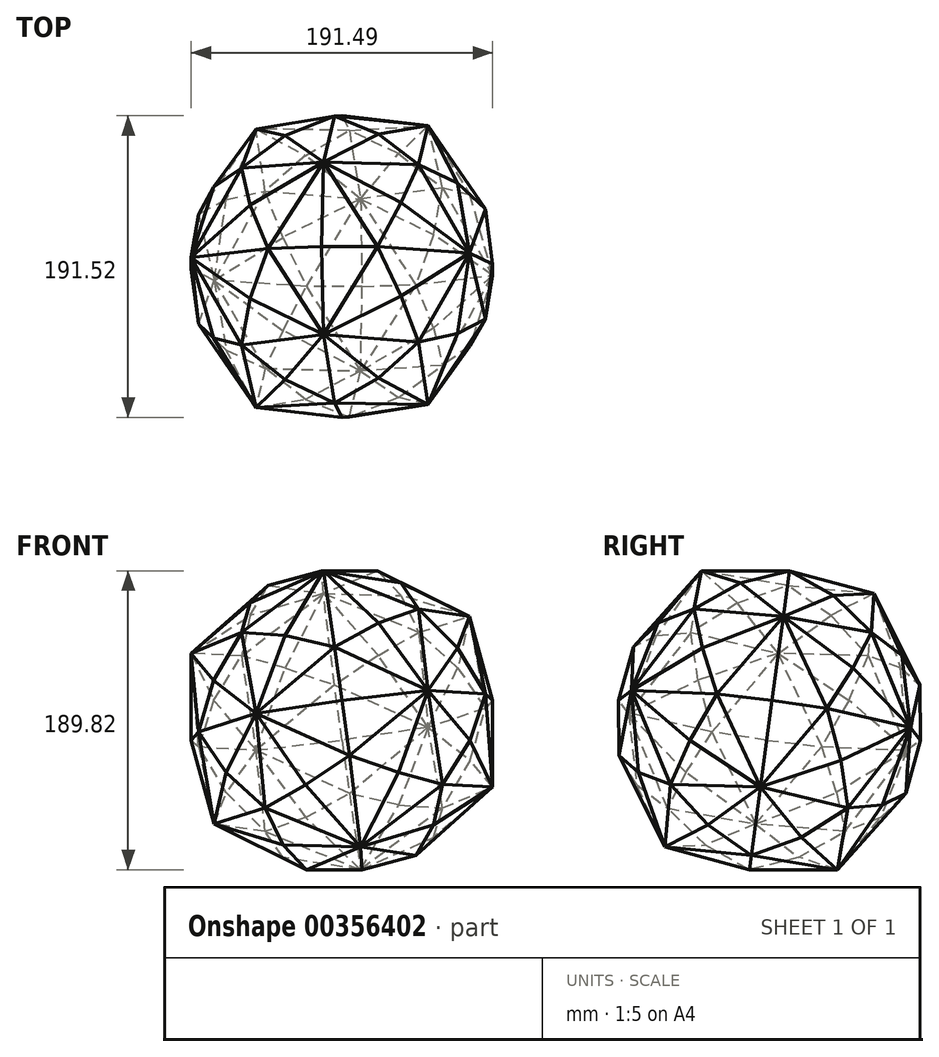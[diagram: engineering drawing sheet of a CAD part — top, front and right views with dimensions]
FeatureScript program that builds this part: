
annotation { "Feature Type Name" : "Feature", "Feature Type Description" : "" }
export const myFeature = defineFeature(function(context is Context, id is Id, definition is map)
    precondition{}
    {
        {
            var Q0;
            Q0=qCreatedBy(makeId("Top.planeOp"),FACE);
            var sketch = newSketch(context, id + "F0", { "sketchPlane" : qUnion([Q0])});
            skLineSegment(sketch, "E0", {"start": v(-0.98, 55.62) * mm, "end": v(-35.41, 0) * mm});
            skLineSegment(sketch, "E1", {"start": v(-35.41, 0) * mm, "end": v(0, 0) * mm});
            skLineSegment(sketch, "E2", {"start": v(0, 0) * mm, "end": v(-0.98, 55.62) * mm});
            skSolve(sketch);
        }
        {
            var Q0;
            Q0=makeQuery(id+"F0.imprint","IMPRINT",FACE,{"disambiguationData":[TD([[makeQuery(id+"F0.imprint","IMPRINT",EDGE,{"derivedFrom":sQuery(id+"F0.wireOp",EDGE,"E0")}),1.0]])]});
            extrude(context, id + "F1", {"entities" : qUnion([Q0]), "depth" : 101.6 * mm, "offsetDistance" : 25.4 * mm, "hasDraft" : true, "draftAngle" : 7.56 * degree, "draftPullDirection" : true});
        }
        {
            var Q0;
            Q0=makeQuery(id+"F1.opExtrude","SWEPT_BODY",BODY,{"disambiguationData":[OSD([sQuery(id+"F0.wireOp",EDGE,"E0"),sQuery(id+"F0.wireOp",EDGE,"E1"),sQuery(id+"F0.wireOp",EDGE,"E2")])]});
            var Q1;
            Q1=makeQuery(id+"F1.opExtrude","SWEPT_FACE",FACE,{"disambiguationData":[OSD([sQuery(id+"F0.wireOp",EDGE,"E0")])]});
            mirror(context, id + "F2", {"operationType" : NewBodyOperationType.ADD, "entities" : qUnion([Q0]), "mirrorPlane" : qUnion([Q1])});
        }
        {
            var Q0;
            Q0=makeQuery(id+"F1.opExtrude","SWEPT_BODY",BODY,{"disambiguationData":[OSD([sQuery(id+"F0.wireOp",EDGE,"E0"),sQuery(id+"F0.wireOp",EDGE,"E1"),sQuery(id+"F0.wireOp",EDGE,"E2")])]});
            var Q1;
            Q1=makeQuery(id+"F1.opExtrude","SWEPT_FACE",FACE,{"disambiguationData":[OSD([sQuery(id+"F0.wireOp",EDGE,"E2")])]});
            mirror(context, id + "F3", {"operationType" : NewBodyOperationType.ADD, "entities" : qUnion([Q0]), "mirrorPlane" : qUnion([Q1])});
        }
        {
            var Q0;
            Q0=makeQuery(id+"F1.opExtrude","SWEPT_BODY",BODY,{"disambiguationData":[OSD([sQuery(id+"F0.wireOp",EDGE,"E0"),sQuery(id+"F0.wireOp",EDGE,"E1"),sQuery(id+"F0.wireOp",EDGE,"E2")])]});
            var Q1;
            Q1=makeQuery(id+"F3.opPattern","COPY",FACE,{"derivedFrom":makeQuery(id+"F2.opPattern","COPY",FACE,{"derivedFrom":makeQuery(id+"F1.opExtrude","SWEPT_FACE",FACE,{"disambiguationData":[OSD([sQuery(id+"F0.wireOp",EDGE,"E2")])]}),"instanceName":"1"}),"instanceName":"1"});
            mirror(context, id + "F4", {"operationType" : NewBodyOperationType.ADD, "entities" : qUnion([Q0]), "mirrorPlane" : qUnion([Q1])});
        }
        {
            var Q0;
            Q0=makeQuery(id+"F1.opExtrude","SWEPT_BODY",BODY,{"disambiguationData":[OSD([sQuery(id+"F0.wireOp",EDGE,"E0"),sQuery(id+"F0.wireOp",EDGE,"E1"),sQuery(id+"F0.wireOp",EDGE,"E2")])]});
            var Q1;
            Q1=makeQuery(id+"F2.opPattern","COPY",FACE,{"derivedFrom":makeQuery(id+"F1.opExtrude","SWEPT_FACE",FACE,{"disambiguationData":[OSD([sQuery(id+"F0.wireOp",EDGE,"E2")])]}),"instanceName":"1"});
            mirror(context, id + "F5", {"operationType" : NewBodyOperationType.ADD, "entities" : qUnion([Q0]), "mirrorPlane" : qUnion([Q1])});
        }
        {
            var Q0;
            Q0=makeQuery(id+"F1.opExtrude","SWEPT_BODY",BODY,{"disambiguationData":[OSD([sQuery(id+"F0.wireOp",EDGE,"E0"),sQuery(id+"F0.wireOp",EDGE,"E1"),sQuery(id+"F0.wireOp",EDGE,"E2")])]});
            var Q1;
            {var subQ0=makeQuery(id+"F1.opExtrude","SWEPT_FACE",FACE,{"disambiguationData":[OSD([sQuery(id+"F0.wireOp",EDGE,"E1")])]});Q1=makeQuery(id+"F3.boolean.opBoolean","MERGE",FACE,{"derivedFrom":[subQ0,makeQuery(id+"F3.opPattern","COPY",FACE,{"derivedFrom":subQ0,"instanceName":"1"})]});}
            mirror(context, id + "F6", {"operationType" : NewBodyOperationType.ADD, "entities" : qUnion([Q0]), "mirrorPlane" : qUnion([Q1])});
        }
        {
            var Q0;
            Q0=makeQuery(id+"F1.opExtrude","SWEPT_BODY",BODY,{"disambiguationData":[OSD([sQuery(id+"F0.wireOp",EDGE,"E0"),sQuery(id+"F0.wireOp",EDGE,"E1"),sQuery(id+"F0.wireOp",EDGE,"E2")])]});
            var Q1;
            {var subQ0=makeQuery(id+"F3.opPattern","COPY",FACE,{"derivedFrom":makeQuery(id+"F2.opPattern","COPY",FACE,{"derivedFrom":makeQuery(id+"F1.opExtrude","SWEPT_FACE",FACE,{"disambiguationData":[OSD([sQuery(id+"F0.wireOp",EDGE,"E1")])]}),"instanceName":"1"}),"instanceName":"1"});Q1=makeQuery(id+"F6.opPattern","COPY",FACE,{"derivedFrom":makeQuery(id+"F4.boolean.opBoolean","MERGE",FACE,{"derivedFrom":[subQ0,makeQuery(id+"F4.opPattern","COPY",FACE,{"derivedFrom":subQ0,"instanceName":"1"})]}),"instanceName":"1"});}
            mirror(context, id + "F7", {"operationType" : NewBodyOperationType.ADD, "entities" : qUnion([Q0]), "mirrorPlane" : qUnion([Q1])});
        }
        {
            var Q0;
            Q0=makeQuery(id+"F1.opExtrude","SWEPT_BODY",BODY,{"disambiguationData":[OSD([sQuery(id+"F0.wireOp",EDGE,"E0"),sQuery(id+"F0.wireOp",EDGE,"E1"),sQuery(id+"F0.wireOp",EDGE,"E2")])]});
            var Q1;
            {var subQ0=makeQuery(id+"F2.opPattern","COPY",FACE,{"derivedFrom":makeQuery(id+"F1.opExtrude","SWEPT_FACE",FACE,{"disambiguationData":[OSD([sQuery(id+"F0.wireOp",EDGE,"E1")])]}),"instanceName":"1"});Q1=makeQuery(id+"F7.opPattern","COPY",FACE,{"derivedFrom":makeQuery(id+"F6.opPattern","COPY",FACE,{"derivedFrom":makeQuery(id+"F5.boolean.opBoolean","MERGE",FACE,{"derivedFrom":[subQ0,makeQuery(id+"F5.opPattern","COPY",FACE,{"derivedFrom":subQ0,"instanceName":"1"})]}),"instanceName":"1"}),"instanceName":"1"});}
            mirror(context, id + "F8", {"operationType" : NewBodyOperationType.ADD, "entities" : qUnion([Q0]), "mirrorPlane" : qUnion([Q1])});
        }
        {
            var Q0;
            Q0=makeQuery(id+"F1.opExtrude","SWEPT_BODY",BODY,{"disambiguationData":[OSD([sQuery(id+"F0.wireOp",EDGE,"E0"),sQuery(id+"F0.wireOp",EDGE,"E1"),sQuery(id+"F0.wireOp",EDGE,"E2")])]});
            var Q1;
            {var subQ0=makeQuery(id+"F2.opPattern","COPY",FACE,{"derivedFrom":makeQuery(id+"F1.opExtrude","SWEPT_FACE",FACE,{"disambiguationData":[OSD([sQuery(id+"F0.wireOp",EDGE,"E1")])]}),"instanceName":"1"});Q1=makeQuery(id+"F8.opPattern","COPY",FACE,{"derivedFrom":makeQuery(id+"F6.opPattern","COPY",FACE,{"derivedFrom":makeQuery(id+"F5.boolean.opBoolean","MERGE",FACE,{"derivedFrom":[subQ0,makeQuery(id+"F5.opPattern","COPY",FACE,{"derivedFrom":subQ0,"instanceName":"1"})]}),"instanceName":"1"}),"instanceName":"1"});}
            mirror(context, id + "F9", {"operationType" : NewBodyOperationType.ADD, "entities" : qUnion([Q0]), "mirrorPlane" : qUnion([Q1])});
        }
        {
            var Q0;
            Q0=makeQuery(id+"F1.opExtrude","SWEPT_BODY",BODY,{"disambiguationData":[OSD([sQuery(id+"F0.wireOp",EDGE,"E0"),sQuery(id+"F0.wireOp",EDGE,"E1"),sQuery(id+"F0.wireOp",EDGE,"E2")])]});
            var Q1;
            {var subQ0=makeQuery(id+"F1.opExtrude","SWEPT_FACE",FACE,{"disambiguationData":[OSD([sQuery(id+"F0.wireOp",EDGE,"E1")])]});Q1=makeQuery(id+"F9.opPattern","COPY",FACE,{"derivedFrom":makeQuery(id+"F8.opPattern","COPY",FACE,{"derivedFrom":makeQuery(id+"F6.opPattern","COPY",FACE,{"derivedFrom":makeQuery(id+"F4.opPattern","COPY",FACE,{"derivedFrom":makeQuery(id+"F3.boolean.opBoolean","MERGE",FACE,{"derivedFrom":[subQ0,makeQuery(id+"F3.opPattern","COPY",FACE,{"derivedFrom":subQ0,"instanceName":"1"})]}),"instanceName":"1"}),"instanceName":"1"}),"instanceName":"1"}),"instanceName":"1"});}
            mirror(context, id + "F10", {"operationType" : NewBodyOperationType.ADD, "entities" : qUnion([Q0]), "mirrorPlane" : qUnion([Q1])});
        }
        {
            var Q0;
            Q0=makeQuery(id+"F1.opExtrude","SWEPT_BODY",BODY,{"disambiguationData":[OSD([sQuery(id+"F0.wireOp",EDGE,"E0"),sQuery(id+"F0.wireOp",EDGE,"E1"),sQuery(id+"F0.wireOp",EDGE,"E2")])]});
            var Q1;
            {var subQ0=makeQuery(id+"F1.opExtrude","SWEPT_FACE",FACE,{"disambiguationData":[OSD([sQuery(id+"F0.wireOp",EDGE,"E1")])]});Q1=makeQuery(id+"F10.opPattern","COPY",FACE,{"derivedFrom":makeQuery(id+"F8.opPattern","COPY",FACE,{"derivedFrom":makeQuery(id+"F6.opPattern","COPY",FACE,{"derivedFrom":makeQuery(id+"F5.boolean.opBoolean","MERGE",FACE,{"derivedFrom":[makeQuery(id+"F4.opPattern","COPY",FACE,{"derivedFrom":makeQuery(id+"F2.opPattern","COPY",FACE,{"derivedFrom":subQ0,"instanceName":"1"}),"instanceName":"1"}),makeQuery(id+"F5.opPattern","COPY",FACE,{"derivedFrom":makeQuery(id+"F3.boolean.opBoolean","MERGE",FACE,{"derivedFrom":[subQ0,makeQuery(id+"F3.opPattern","COPY",FACE,{"derivedFrom":subQ0,"instanceName":"1"})]}),"instanceName":"1"})]}),"instanceName":"1"}),"instanceName":"1"}),"instanceName":"1"});}
            mirror(context, id + "F11", {"operationType" : NewBodyOperationType.ADD, "entities" : qUnion([Q0]), "mirrorPlane" : qUnion([Q1])});
        }
        {
            var Q0;
            Q0=makeQuery(id+"F1.opExtrude","SWEPT_BODY",BODY,{"disambiguationData":[OSD([sQuery(id+"F0.wireOp",EDGE,"E0"),sQuery(id+"F0.wireOp",EDGE,"E1"),sQuery(id+"F0.wireOp",EDGE,"E2")])]});
            var Q1;
            {var subQ0=makeQuery(id+"F1.opExtrude","SWEPT_FACE",FACE,{"disambiguationData":[OSD([sQuery(id+"F0.wireOp",EDGE,"E1")])]});Q1=makeQuery(id+"F8.opPattern","COPY",FACE,{"derivedFrom":makeQuery(id+"F7.opPattern","COPY",FACE,{"derivedFrom":makeQuery(id+"F6.opPattern","COPY",FACE,{"derivedFrom":makeQuery(id+"F4.opPattern","COPY",FACE,{"derivedFrom":makeQuery(id+"F3.boolean.opBoolean","MERGE",FACE,{"derivedFrom":[subQ0,makeQuery(id+"F3.opPattern","COPY",FACE,{"derivedFrom":subQ0,"instanceName":"1"})]}),"instanceName":"1"}),"instanceName":"1"}),"instanceName":"1"}),"instanceName":"1"});}
            mirror(context, id + "F12", {"operationType" : NewBodyOperationType.ADD, "entities" : qUnion([Q0]), "mirrorPlane" : qUnion([Q1])});
        }
    });
